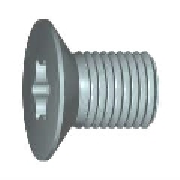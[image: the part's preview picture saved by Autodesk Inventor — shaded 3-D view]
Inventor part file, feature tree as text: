
AUTODESK INVENTOR PART (.ipt)
format: ipt  version: 2022 (Build 260153000, 153)  size: 218,112 bytes
history: native  units: mm
features: sketch x2, revolve x1, thread x1, chamfer x1, extrude x1, pattern_circular x1, fillet x1
ambient origin geometry x8: Origin, YZ Plane, XZ Plane, XY Plane, X Axis, Y Axis, Z Axis, Center Point
bodies: Solid1 (feature_tree)
feature tree (8):
  revolve  "Revolution1"  Angle=90.0deg
  thread  "Thread1"  [1 undecoded]
  chamfer  "Chamfer1"  Distance=0.2mm Angle=45.0deg
  extrude  "Extrusion1"  Depth=0.25mm
  pattern_circular  "Circular Pattern1"  Angle=30.0deg  [1 undecoded]
  fillet  "Fillet1"  [1 undecoded]
  sketch  "Sketch1"  dims[d2=25.0mm d11=90.0deg d12=20.55mm d13=0.0mm d14=0.2mm d15=2.0mm d16=45.0deg]
  sketch  "Sketch2"  dims[d17=5.6mm d18=3.92mm d19=30.0deg d20=30.0deg d21=14.532034mm d22=2.22mm d23=0.0mm d24=60.0mm d25=360.0deg d27=0.6mm d52=45.0deg d54=0.0mm d55=0.0mm d56=0.0mm d57=4.2mm d58=90.0deg d60=13.2mm d61=0.25mm d62=6.0mm]
note: 3 required parameter values undecoded (feature->parameter linkage not recoverable at this tier; creation-order binding heuristic only, values carry confidence <= 0.55)
